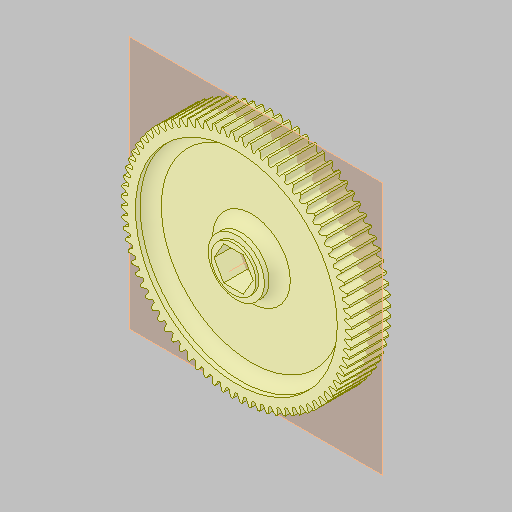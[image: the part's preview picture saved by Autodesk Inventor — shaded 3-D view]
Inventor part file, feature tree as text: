
AUTODESK INVENTOR PART (.ipt)
format: ipt  version: 2023.4 (Build 274418000, 418)  size: 724,992 bytes
history: native  units: in
note: dims shown in document units (in); Inventor stores cm internally (conversion verified against a paired STEP export)
features: mirror x1
ambient origin geometry x8: Origin, YZ Plane, XZ Plane, XY Plane, X Axis, Y Axis, Z Axis, Center Point
bodies: Solid1 (feature_tree)
feature tree (1):
  mirror  "Mirror1"
